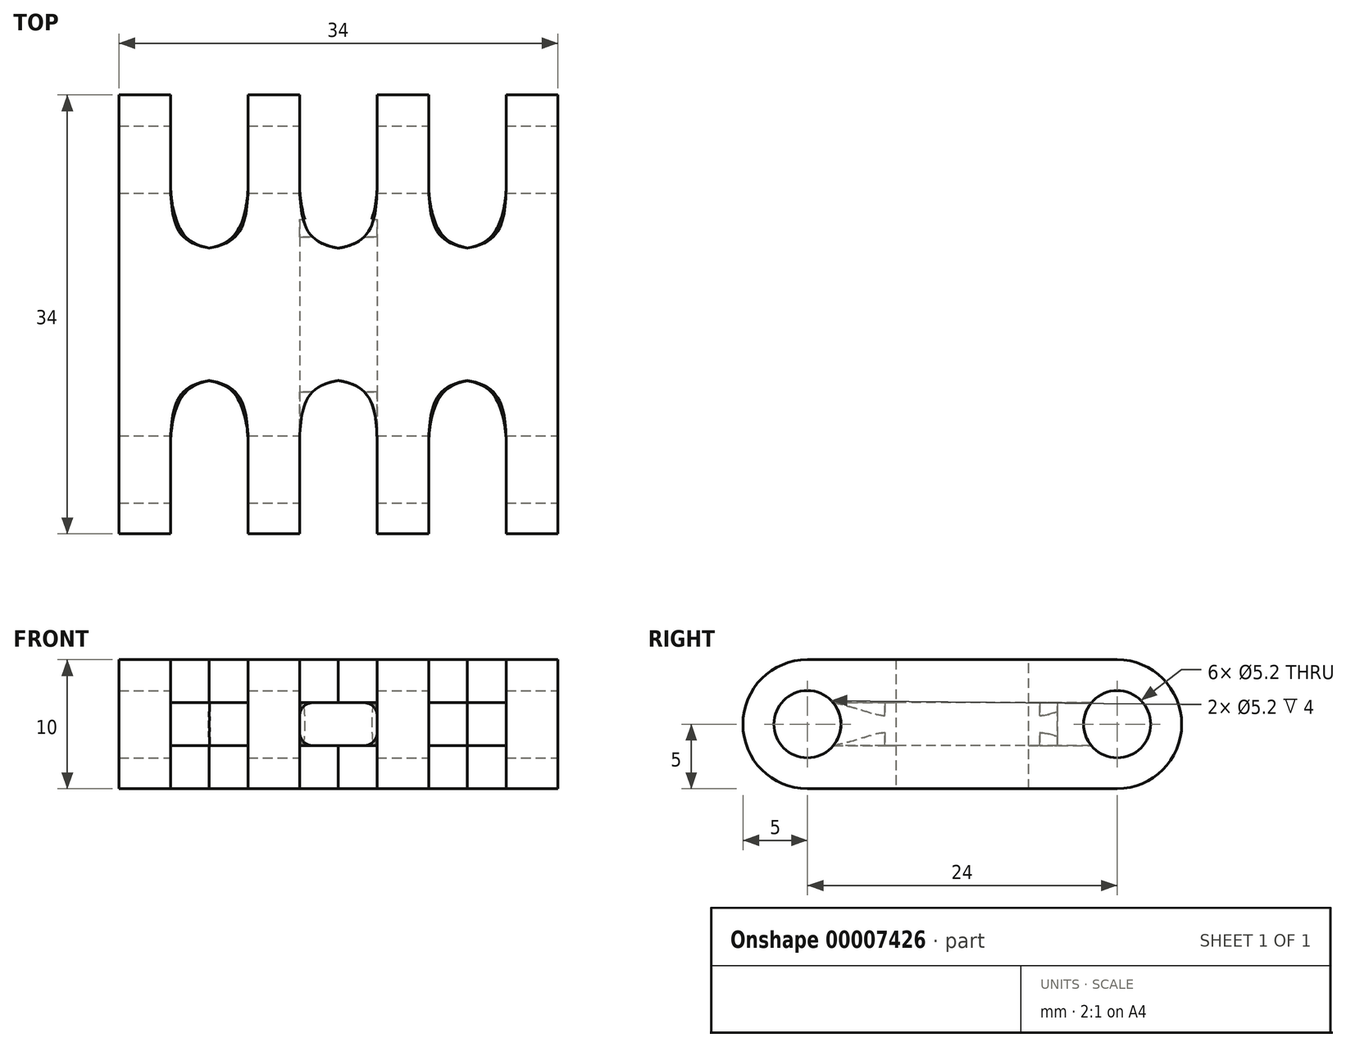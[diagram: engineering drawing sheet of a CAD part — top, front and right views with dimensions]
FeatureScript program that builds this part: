
annotation { "Feature Type Name" : "Feature", "Feature Type Description" : "" }
export const myFeature = defineFeature(function(context is Context, id is Id, definition is map)
    precondition{}
    {
        {
            var Q0;
            Q0=qCreatedBy(makeId("Front.planeOp"),FACE);
            var sketch = newSketch(context, id + "F0", { "sketchPlane" : qUnion([Q0])});
            skLineSegment(sketch, "E0.bottom", {"start": v(-16.45, 10) * mm, "end": v(17.55, 10) * mm});
            skLineSegment(sketch, "E0.top", {"start": v(-16.45, 0) * mm, "end": v(17.55, 0) * mm});
            skLineSegment(sketch, "E0.left", {"start": v(-16.45, 10) * mm, "end": v(-16.45, 0) * mm});
            skLineSegment(sketch, "E0.right", {"start": v(17.55, 10) * mm, "end": v(17.55, 0) * mm});
            skSolve(sketch);
        }
        {
            var Q0;
            Q0=makeQuery(id+"F0.imprint","IMPRINT",FACE,{"disambiguationData":[TD([[makeQuery(id+"F0.imprint","IMPRINT",EDGE,{"derivedFrom":sQuery(id+"F0.wireOp",EDGE,"E0.bottom")}),-1.0]])]});
            extrude(context, id + "F1", {"entities" : qUnion([Q0]), "depth" : 10 * mm});
        }
        {
            var Q0;
            {var subQ0=sQuery(id+"F0.wireOp",EDGE,"E0.bottom");var subQ1=sQuery(id+"F0.wireOp",EDGE,"E0.top");Q0=makeQuery(id+"F4.boolean.opBoolean","SPLIT",FACE,{"disambiguationData":[TD([makeQuery(id+"F4.opExtrude","SWEPT_FACE",FACE,{"disambiguationData":[OSD([sQuery(id+"F3.wireOp",EDGE,"E3.right")])]})])],"derivedFrom":makeQuery(id+"F1.opExtrude","CAP_FACE",FACE,{"disambiguationData":[OSD([subQ0,subQ1,sQuery(id+"F0.wireOp",EDGE,"E0.left"),sQuery(id+"F0.wireOp",EDGE,"E0.right")])],"isStart":false})});}
            cPlane(context, id + "F2", {"entities" : qUnion([Q0]), "cplaneType" : CPlaneType.OFFSET, "offset" : 5 * mm, "oppositeDirection" : true, "width" : 150 * mm, "height" : 150 * mm});
        }
        {
            var Q0;
            Q0=qCreatedBy(id+"F2.planeOp",FACE);
            var sketch = newSketch(context, id + "F3", { "sketchPlane" : qUnion([Q0])});
            skLineSegment(sketch, "E1.bottom", {"start": v(-16.45, 10) * mm, "end": v(-12.45, 10) * mm});
            skLineSegment(sketch, "E1.top", {"start": v(-16.45, 0) * mm, "end": v(-12.45, 0) * mm});
            skLineSegment(sketch, "E1.left", {"start": v(-16.45, 10) * mm, "end": v(-16.45, 0) * mm});
            skLineSegment(sketch, "E1.right", {"start": v(-12.45, 10) * mm, "end": v(-12.45, 0) * mm});
            skLineSegment(sketch, "E2.bottom", {"start": v(-6.45, 10) * mm, "end": v(-2.45, 10) * mm});
            skLineSegment(sketch, "E2.top", {"start": v(-6.45, 0) * mm, "end": v(-2.45, 0) * mm});
            skLineSegment(sketch, "E2.left", {"start": v(-6.45, 10) * mm, "end": v(-6.45, 0) * mm});
            skLineSegment(sketch, "E2.right", {"start": v(-2.45, 10) * mm, "end": v(-2.45, 0) * mm});
            skLineSegment(sketch, "E3.bottom", {"start": v(17.55, 10) * mm, "end": v(13.55, 10) * mm});
            skLineSegment(sketch, "E3.top", {"start": v(17.55, 0) * mm, "end": v(13.55, 0) * mm});
            skLineSegment(sketch, "E3.left", {"start": v(17.55, 10) * mm, "end": v(17.55, 0) * mm});
            skLineSegment(sketch, "E3.right", {"start": v(13.55, 10) * mm, "end": v(13.55, 0) * mm});
            skLineSegment(sketch, "E4.bottom", {"start": v(3.55, 10) * mm, "end": v(7.55, 10) * mm});
            skLineSegment(sketch, "E4.top", {"start": v(3.55, 0) * mm, "end": v(7.55, 0) * mm});
            skLineSegment(sketch, "E4.left", {"start": v(3.55, 10) * mm, "end": v(3.55, 0) * mm});
            skLineSegment(sketch, "E4.right", {"start": v(7.55, 10) * mm, "end": v(7.55, 0) * mm});
            skSolve(sketch);
        }
        {
            var Q0;
            Q0=makeQuery(id+"F3.imprint","IMPRINT",FACE,{"disambiguationData":[TD([[makeQuery(id+"F3.imprint","IMPRINT",EDGE,{"derivedFrom":sQuery(id+"F3.wireOp",EDGE,"E1.bottom")}),-1.0]])]});
            var Q1;
            Q1=makeQuery(id+"F3.imprint","IMPRINT",FACE,{"disambiguationData":[TD([[makeQuery(id+"F3.imprint","IMPRINT",EDGE,{"derivedFrom":sQuery(id+"F3.wireOp",EDGE,"E2.bottom")}),-1.0]])]});
            var Q2;
            Q2=makeQuery(id+"F3.imprint","IMPRINT",FACE,{"disambiguationData":[TD([[makeQuery(id+"F3.imprint","IMPRINT",EDGE,{"derivedFrom":sQuery(id+"F3.wireOp",EDGE,"E4.bottom")}),-1.0]])]});
            var Q3;
            Q3=makeQuery(id+"F3.imprint","IMPRINT",FACE,{"disambiguationData":[TD([[makeQuery(id+"F3.imprint","IMPRINT",EDGE,{"derivedFrom":sQuery(id+"F3.wireOp",EDGE,"E3.bottom")}),-1.0]])]});
            var Q4;
            Q4=makeQuery(id+"F3.imprint","IMPRINT",FACE,{"disambiguationData":[TD([[makeQuery(id+"F3.imprint","IMPRINT",EDGE,{"derivedFrom":sQuery(id+"F3.wireOp",EDGE,"E3.bottom")}),1.0]])]});
            extrude(context, id + "F4", {"entities" : qUnion([Q0, Q1, Q2, Q3, Q4]), "operationType" : NewBodyOperationType.ADD, "depth" : 24 * mm, "symmetric" : true});
        }
        {
            var Q0;
            Q0=makeQuery(id+"F4.boolean.opBoolean","MERGE",FACE,{"derivedFrom":[makeQuery(id+"F1.opExtrude","SWEPT_FACE",FACE,{"disambiguationData":[OSD([sQuery(id+"F0.wireOp",EDGE,"E0.right")])]}),makeQuery(id+"F4.opExtrude","SWEPT_FACE",FACE,{"disambiguationData":[OSD([sQuery(id+"F3.wireOp",EDGE,"E3.left")])]})]});
            var sketch = newSketch(context, id + "F5", { "sketchPlane" : qUnion([Q0])});
            skCircle(sketch, "E5", {"center": v(-17, 5) * mm, "radius": 5 * mm});
            skCircle(sketch, "E6", {"center": v(7, 5) * mm, "radius": 5 * mm});
            skSolve(sketch);
        }
        {
            var Q0;
            {var subQ0=sQuery(id+"F3.wireOp",EDGE,"E3.left");var subQ1=makeQuery(id+"F4.opExtrude","CAP_EDGE",EDGE,{"disambiguationData":[OSD([subQ0])],"isStart":false});Q0=makeQuery(id+"F5.imprint","IMPRINT",FACE,{"disambiguationData":[TD([[makeQuery(id+"F5.imprint","IMPRINT",EDGE,{"derivedFrom":subQ1}),-1.0]])]});}
            var Q1;
            {var subQ0=sQuery(id+"F3.wireOp",EDGE,"E3.left");var subQ1=makeQuery(id+"F4.opExtrude","CAP_EDGE",EDGE,{"disambiguationData":[OSD([subQ0])],"isStart":true});Q1=makeQuery(id+"F5.imprint","IMPRINT",FACE,{"disambiguationData":[TD([[makeQuery(id+"F5.imprint","IMPRINT",EDGE,{"derivedFrom":subQ1}),1.0]])]});}
            var Q2;
            {var subQ0=sQuery(id+"F3.wireOp",EDGE,"E3.left");var subQ1=makeQuery(id+"F4.opExtrude","CAP_EDGE",EDGE,{"disambiguationData":[OSD([subQ0])],"isStart":true});Q2=makeQuery(id+"F5.imprint","IMPRINT",FACE,{"disambiguationData":[TD([[makeQuery(id+"F5.imprint","IMPRINT",EDGE,{"derivedFrom":subQ1}),-1.0]])]});}
            var Q3;
            {var subQ0=sQuery(id+"F3.wireOp",EDGE,"E3.left");var subQ1=makeQuery(id+"F4.opExtrude","CAP_EDGE",EDGE,{"disambiguationData":[OSD([subQ0])],"isStart":false});Q3=makeQuery(id+"F5.imprint","IMPRINT",FACE,{"disambiguationData":[TD([[makeQuery(id+"F5.imprint","IMPRINT",EDGE,{"derivedFrom":subQ1}),1.0]])]});}
            extrude(context, id + "F6", {"entities" : qUnion([Q0, Q1, Q2, Q3]), "operationType" : NewBodyOperationType.ADD, "oppositeDirection" : true, "depth" : 34 * mm});
        }
        {
            var Q0;
            Q0=makeQuery(id+"F4.boolean.opBoolean","MERGE",FACE,{"derivedFrom":[makeQuery(id+"F1.opExtrude","SWEPT_FACE",FACE,{"disambiguationData":[OSD([sQuery(id+"F0.wireOp",EDGE,"E0.bottom")])]}),makeQuery(id+"F4.opExtrude","SWEPT_FACE",FACE,{"disambiguationData":[OSD([sQuery(id+"F3.wireOp",EDGE,"E1.bottom")])]}),makeQuery(id+"F4.opExtrude","SWEPT_FACE",FACE,{"disambiguationData":[OSD([sQuery(id+"F3.wireOp",EDGE,"E2.bottom")])]}),makeQuery(id+"F4.opExtrude","SWEPT_FACE",FACE,{"disambiguationData":[OSD([sQuery(id+"F3.wireOp",EDGE,"E3.bottom")])]}),makeQuery(id+"F4.opExtrude","SWEPT_FACE",FACE,{"disambiguationData":[OSD([sQuery(id+"F3.wireOp",EDGE,"E4.bottom")])]})]});
            var sketch = newSketch(context, id + "F7", { "sketchPlane" : qUnion([Q0])});
            skLineSegment(sketch, "E7.bottom", {"start": v(-12.45, -10) * mm, "end": v(-6.45, -10) * mm});
            skLineSegment(sketch, "E7.top", {"start": v(-12.45, -24.03) * mm, "end": v(-6.45, -24.03) * mm});
            skLineSegment(sketch, "E7.left", {"start": v(-12.45, -10) * mm, "end": v(-12.45, -24.03) * mm});
            skLineSegment(sketch, "E7.right", {"start": v(-6.45, -10) * mm, "end": v(-6.45, -24.03) * mm});
            skLineSegment(sketch, "E8.bottom", {"start": v(-2.45, -10) * mm, "end": v(3.55, -10) * mm});
            skLineSegment(sketch, "E8.top", {"start": v(-2.45, -24.03) * mm, "end": v(3.55, -24.03) * mm});
            skLineSegment(sketch, "E8.left", {"start": v(-2.45, -10) * mm, "end": v(-2.45, -24.03) * mm});
            skLineSegment(sketch, "E8.right", {"start": v(3.55, -10) * mm, "end": v(3.55, -24.03) * mm});
            skLineSegment(sketch, "E9.bottom", {"start": v(7.55, -10) * mm, "end": v(13.55, -10) * mm});
            skLineSegment(sketch, "E9.top", {"start": v(7.55, -24.03) * mm, "end": v(13.55, -24.03) * mm});
            skLineSegment(sketch, "E9.left", {"start": v(7.55, -10) * mm, "end": v(7.55, -24.03) * mm});
            skLineSegment(sketch, "E9.right", {"start": v(13.55, -10) * mm, "end": v(13.55, -24.03) * mm});
            skLineSegment(sketch, "E10.bottom", {"start": v(-12.45, 0) * mm, "end": v(-6.45, 0) * mm});
            skLineSegment(sketch, "E10.top", {"start": v(-12.45, 16.74) * mm, "end": v(-6.45, 16.74) * mm});
            skLineSegment(sketch, "E10.left", {"start": v(-12.45, 0) * mm, "end": v(-12.45, 16.74) * mm});
            skLineSegment(sketch, "E10.right", {"start": v(-6.45, 0) * mm, "end": v(-6.45, 16.74) * mm});
            skLineSegment(sketch, "E11.bottom", {"start": v(-2.45, 0) * mm, "end": v(3.55, 0) * mm});
            skLineSegment(sketch, "E11.top", {"start": v(-2.45, 16.6) * mm, "end": v(3.55, 16.6) * mm});
            skLineSegment(sketch, "E11.left", {"start": v(-2.45, 0) * mm, "end": v(-2.45, 16.6) * mm});
            skLineSegment(sketch, "E11.right", {"start": v(3.55, 0) * mm, "end": v(3.55, 16.6) * mm});
            skLineSegment(sketch, "E12.bottom", {"start": v(7.55, 0) * mm, "end": v(13.55, 0) * mm});
            skLineSegment(sketch, "E12.top", {"start": v(7.55, 16.45) * mm, "end": v(13.55, 16.45) * mm});
            skLineSegment(sketch, "E12.left", {"start": v(7.55, 0) * mm, "end": v(7.55, 16.45) * mm});
            skLineSegment(sketch, "E12.right", {"start": v(13.55, 0) * mm, "end": v(13.55, 16.45) * mm});
            skSolve(sketch);
        }
        {
            var Q0;
            {var subQ2=sQuery(id+"F7.wireOp",EDGE,"E10.bottom");Q0=makeQuery(id+"F7.imprint","IMPRINT",FACE,{"disambiguationData":[TD([[makeQuery(id+"F7.imprint","IMPRINT",EDGE,{"derivedFrom":subQ2}),1.0]])]});}
            var Q1;
            {var subQ2=sQuery(id+"F7.wireOp",EDGE,"E11.bottom");Q1=makeQuery(id+"F7.imprint","IMPRINT",FACE,{"disambiguationData":[TD([[makeQuery(id+"F7.imprint","IMPRINT",EDGE,{"derivedFrom":subQ2}),1.0]])]});}
            var Q2;
            {var subQ2=sQuery(id+"F7.wireOp",EDGE,"E12.bottom");Q2=makeQuery(id+"F7.imprint","IMPRINT",FACE,{"disambiguationData":[TD([[makeQuery(id+"F7.imprint","IMPRINT",EDGE,{"derivedFrom":subQ2}),1.0]])]});}
            var Q3;
            {var subQ2=sQuery(id+"F7.wireOp",EDGE,"E9.bottom");Q3=makeQuery(id+"F7.imprint","IMPRINT",FACE,{"disambiguationData":[TD([[makeQuery(id+"F7.imprint","IMPRINT",EDGE,{"derivedFrom":subQ2}),-1.0]])]});}
            var Q4;
            {var subQ2=sQuery(id+"F7.wireOp",EDGE,"E8.bottom");Q4=makeQuery(id+"F7.imprint","IMPRINT",FACE,{"disambiguationData":[TD([[makeQuery(id+"F7.imprint","IMPRINT",EDGE,{"derivedFrom":subQ2}),-1.0]])]});}
            var Q5;
            {var subQ2=sQuery(id+"F7.wireOp",EDGE,"E7.bottom");Q5=makeQuery(id+"F7.imprint","IMPRINT",FACE,{"disambiguationData":[TD([[makeQuery(id+"F7.imprint","IMPRINT",EDGE,{"derivedFrom":subQ2}),-1.0]])]});}
            extrude(context, id + "F8", {"entities" : qUnion([Q0, Q1, Q2, Q3, Q4, Q5]), "operationType" : NewBodyOperationType.REMOVE, "oppositeDirection" : true, "depth" : 25 * mm});
        }
        {
            var Q0;
            Q0=makeQuery(id+"F6.boolean.opBoolean","MERGE",FACE,{"derivedFrom":[makeQuery(id+"F4.boolean.opBoolean","MERGE",FACE,{"derivedFrom":[makeQuery(id+"F1.opExtrude","SWEPT_FACE",FACE,{"disambiguationData":[OSD([sQuery(id+"F0.wireOp",EDGE,"E0.right")])]}),makeQuery(id+"F4.opExtrude","SWEPT_FACE",FACE,{"disambiguationData":[OSD([sQuery(id+"F3.wireOp",EDGE,"E3.left")])]})]}),makeQuery(id+"F6.opExtrude","CAP_FACE",FACE,{"disambiguationData":[OSD([sQuery(id+"F5.wireOp",EDGE,"E5")])],"isStart":true}),makeQuery(id+"F6.opExtrude","CAP_FACE",FACE,{"disambiguationData":[OSD([sQuery(id+"F5.wireOp",EDGE,"E6")])],"isStart":true})]});
            var sketch = newSketch(context, id + "F9", { "sketchPlane" : qUnion([Q0])});
            skCircle(sketch, "E13", {"center": v(7, 5) * mm, "radius": 5 * mm});
            skCircle(sketch, "E14", {"center": v(-17, 5) * mm, "radius": 5 * mm});
            skCircle(sketch, "E15", {"center": v(-17, 5) * mm, "radius": 2.6 * mm});
            skCircle(sketch, "E16", {"center": v(7, 5) * mm, "radius": 2.6 * mm});
            skSolve(sketch);
        }
        {
            var Q0;
            Q0=makeQuery(id+"F9.imprint","IMPRINT",FACE,{"disambiguationData":[TD([[makeQuery(id+"F9.imprint","IMPRINT",EDGE,{"derivedFrom":sQuery(id+"F9.wireOp",EDGE,"E15")}),1.0]])]});
            var Q1;
            Q1=makeQuery(id+"F9.imprint","IMPRINT",FACE,{"disambiguationData":[TD([[makeQuery(id+"F9.imprint","IMPRINT",EDGE,{"derivedFrom":sQuery(id+"F9.wireOp",EDGE,"E16")}),1.0]])]});
            extrude(context, id + "F10", {"entities" : qUnion([Q0, Q1]), "operationType" : NewBodyOperationType.REMOVE, "endBound" : BoundingType.THROUGH_ALL, "oppositeDirection" : true, "depth" : 25 * mm});
        }
        {
            var Q0;
            Q0=makeQuery(id+"F4.boolean.opBoolean","INTERSECT",EDGE,{"derivedFrom":[makeQuery(id+"F1.opExtrude","CAP_FACE",FACE,{"disambiguationData":[OSD([sQuery(id+"F0.wireOp",EDGE,"E0.bottom"),sQuery(id+"F0.wireOp",EDGE,"E0.top"),sQuery(id+"F0.wireOp",EDGE,"E0.left"),sQuery(id+"F0.wireOp",EDGE,"E0.right")])],"isStart":true}),makeQuery(id+"F4.opExtrude","SWEPT_FACE",FACE,{"disambiguationData":[OSD([sQuery(id+"F3.wireOp",EDGE,"E3.right")])]})]});
            var Q1;
            Q1=makeQuery(id+"F4.boolean.opBoolean","INTERSECT",EDGE,{"derivedFrom":[makeQuery(id+"F1.opExtrude","CAP_FACE",FACE,{"disambiguationData":[OSD([sQuery(id+"F0.wireOp",EDGE,"E0.bottom"),sQuery(id+"F0.wireOp",EDGE,"E0.top"),sQuery(id+"F0.wireOp",EDGE,"E0.left"),sQuery(id+"F0.wireOp",EDGE,"E0.right")])],"isStart":true}),makeQuery(id+"F4.opExtrude","SWEPT_FACE",FACE,{"disambiguationData":[OSD([sQuery(id+"F3.wireOp",EDGE,"E4.right")])]})]});
            var Q2;
            Q2=makeQuery(id+"F4.boolean.opBoolean","INTERSECT",EDGE,{"derivedFrom":[makeQuery(id+"F1.opExtrude","CAP_FACE",FACE,{"disambiguationData":[OSD([sQuery(id+"F0.wireOp",EDGE,"E0.bottom"),sQuery(id+"F0.wireOp",EDGE,"E0.top"),sQuery(id+"F0.wireOp",EDGE,"E0.left"),sQuery(id+"F0.wireOp",EDGE,"E0.right")])],"isStart":true}),makeQuery(id+"F4.opExtrude","SWEPT_FACE",FACE,{"disambiguationData":[OSD([sQuery(id+"F3.wireOp",EDGE,"E2.right")])]})]});
            var Q3;
            Q3=makeQuery(id+"F4.boolean.opBoolean","INTERSECT",EDGE,{"derivedFrom":[makeQuery(id+"F1.opExtrude","CAP_FACE",FACE,{"disambiguationData":[OSD([sQuery(id+"F0.wireOp",EDGE,"E0.bottom"),sQuery(id+"F0.wireOp",EDGE,"E0.top"),sQuery(id+"F0.wireOp",EDGE,"E0.left"),sQuery(id+"F0.wireOp",EDGE,"E0.right")])],"isStart":true}),makeQuery(id+"F4.opExtrude","SWEPT_FACE",FACE,{"disambiguationData":[OSD([sQuery(id+"F3.wireOp",EDGE,"E4.left")])]})]});
            var Q4;
            Q4=makeQuery(id+"F4.boolean.opBoolean","INTERSECT",EDGE,{"derivedFrom":[makeQuery(id+"F1.opExtrude","CAP_FACE",FACE,{"disambiguationData":[OSD([sQuery(id+"F0.wireOp",EDGE,"E0.bottom"),sQuery(id+"F0.wireOp",EDGE,"E0.top"),sQuery(id+"F0.wireOp",EDGE,"E0.left"),sQuery(id+"F0.wireOp",EDGE,"E0.right")])],"isStart":true}),makeQuery(id+"F4.opExtrude","SWEPT_FACE",FACE,{"disambiguationData":[OSD([sQuery(id+"F3.wireOp",EDGE,"E2.left")])]})]});
            var Q5;
            Q5=makeQuery(id+"F4.boolean.opBoolean","INTERSECT",EDGE,{"derivedFrom":[makeQuery(id+"F1.opExtrude","CAP_FACE",FACE,{"disambiguationData":[OSD([sQuery(id+"F0.wireOp",EDGE,"E0.bottom"),sQuery(id+"F0.wireOp",EDGE,"E0.top"),sQuery(id+"F0.wireOp",EDGE,"E0.left"),sQuery(id+"F0.wireOp",EDGE,"E0.right")])],"isStart":true}),makeQuery(id+"F4.opExtrude","SWEPT_FACE",FACE,{"disambiguationData":[OSD([sQuery(id+"F3.wireOp",EDGE,"E1.right")])]})]});
            var Q6;
            Q6=makeQuery(id+"F4.boolean.opBoolean","INTERSECT",EDGE,{"derivedFrom":[makeQuery(id+"F1.opExtrude","CAP_FACE",FACE,{"disambiguationData":[OSD([sQuery(id+"F0.wireOp",EDGE,"E0.bottom"),sQuery(id+"F0.wireOp",EDGE,"E0.top"),sQuery(id+"F0.wireOp",EDGE,"E0.left"),sQuery(id+"F0.wireOp",EDGE,"E0.right")])],"isStart":false}),makeQuery(id+"F4.opExtrude","SWEPT_FACE",FACE,{"disambiguationData":[OSD([sQuery(id+"F3.wireOp",EDGE,"E4.right")])]})]});
            var Q7;
            Q7=makeQuery(id+"F4.boolean.opBoolean","INTERSECT",EDGE,{"derivedFrom":[makeQuery(id+"F1.opExtrude","CAP_FACE",FACE,{"disambiguationData":[OSD([sQuery(id+"F0.wireOp",EDGE,"E0.bottom"),sQuery(id+"F0.wireOp",EDGE,"E0.top"),sQuery(id+"F0.wireOp",EDGE,"E0.left"),sQuery(id+"F0.wireOp",EDGE,"E0.right")])],"isStart":false}),makeQuery(id+"F4.opExtrude","SWEPT_FACE",FACE,{"disambiguationData":[OSD([sQuery(id+"F3.wireOp",EDGE,"E2.right")])]})]});
            var Q8;
            Q8=makeQuery(id+"F4.boolean.opBoolean","INTERSECT",EDGE,{"derivedFrom":[makeQuery(id+"F1.opExtrude","CAP_FACE",FACE,{"disambiguationData":[OSD([sQuery(id+"F0.wireOp",EDGE,"E0.bottom"),sQuery(id+"F0.wireOp",EDGE,"E0.top"),sQuery(id+"F0.wireOp",EDGE,"E0.left"),sQuery(id+"F0.wireOp",EDGE,"E0.right")])],"isStart":false}),makeQuery(id+"F4.opExtrude","SWEPT_FACE",FACE,{"disambiguationData":[OSD([sQuery(id+"F3.wireOp",EDGE,"E1.right")])]})]});
            var Q9;
            Q9=makeQuery(id+"F4.boolean.opBoolean","INTERSECT",EDGE,{"derivedFrom":[makeQuery(id+"F1.opExtrude","CAP_FACE",FACE,{"disambiguationData":[OSD([sQuery(id+"F0.wireOp",EDGE,"E0.bottom"),sQuery(id+"F0.wireOp",EDGE,"E0.top"),sQuery(id+"F0.wireOp",EDGE,"E0.left"),sQuery(id+"F0.wireOp",EDGE,"E0.right")])],"isStart":false}),makeQuery(id+"F4.opExtrude","SWEPT_FACE",FACE,{"disambiguationData":[OSD([sQuery(id+"F3.wireOp",EDGE,"E2.left")])]})]});
            var Q10;
            Q10=makeQuery(id+"F4.boolean.opBoolean","INTERSECT",EDGE,{"derivedFrom":[makeQuery(id+"F1.opExtrude","CAP_FACE",FACE,{"disambiguationData":[OSD([sQuery(id+"F0.wireOp",EDGE,"E0.bottom"),sQuery(id+"F0.wireOp",EDGE,"E0.top"),sQuery(id+"F0.wireOp",EDGE,"E0.left"),sQuery(id+"F0.wireOp",EDGE,"E0.right")])],"isStart":false}),makeQuery(id+"F4.opExtrude","SWEPT_FACE",FACE,{"disambiguationData":[OSD([sQuery(id+"F3.wireOp",EDGE,"E4.left")])]})]});
            var Q11;
            Q11=makeQuery(id+"F4.boolean.opBoolean","INTERSECT",EDGE,{"derivedFrom":[makeQuery(id+"F1.opExtrude","CAP_FACE",FACE,{"disambiguationData":[OSD([sQuery(id+"F0.wireOp",EDGE,"E0.bottom"),sQuery(id+"F0.wireOp",EDGE,"E0.top"),sQuery(id+"F0.wireOp",EDGE,"E0.left"),sQuery(id+"F0.wireOp",EDGE,"E0.right")])],"isStart":false}),makeQuery(id+"F4.opExtrude","SWEPT_FACE",FACE,{"disambiguationData":[OSD([sQuery(id+"F3.wireOp",EDGE,"E3.right")])]})]});
            fillet(context, id + "F11", {"entities" : qUnion([Q0, Q1, Q2, Q3, Q4, Q5, Q6, Q7, Q8, Q9, Q10, Q11]), "radius" : 5 * mm, "tangentPropagation" : true, "rho" : .6, "crossSection" : FilletCrossSection.CONIC, "allowEdgeOverflow" : false});
        }
        {
            var Q0;
            Q0=makeQuery(id+"F1.opExtrude","SWEPT_BODY",BODY,{"disambiguationData":[OSD([sQuery(id+"F0.wireOp",EDGE,"E0.bottom"),sQuery(id+"F0.wireOp",EDGE,"E0.top"),sQuery(id+"F0.wireOp",EDGE,"E0.left"),sQuery(id+"F0.wireOp",EDGE,"E0.right")])]});
            transform(context, id + "F12", {"entities" : qUnion([Q0]), "transformType" : TransformType.TRANSLATION_3D, "dx" : -.533 * mm, "dy" : 5.13 * mm, "dz" : 0 * mm, "makeCopy" : false});
        }
        {
            var Q0;
            Q0=qCreatedBy(id+"F2.planeOp",FACE);
            var sketch = newSketch(context, id + "F13", { "sketchPlane" : qUnion([Q0])});
            skFitSpline(sketch, "E17.0.0", {"points": [v(0.02, 6.66) * mm, v(-0.98, 6.66) * mm, v(-1.98, 6.66) * mm, v(-2.98, 6.66) * mm]});
            skFitSpline(sketch, "E17.0.1", {"points": [v(-2.98, 6.66) * mm, v(-2.98, 5.55) * mm, v(-2.98, 4.45) * mm, v(-2.98, 3.34) * mm]});
            skFitSpline(sketch, "E17.0.2", {"points": [v(-2.98, 3.34) * mm, v(-1.98, 3.34) * mm, v(-0.98, 3.34) * mm, v(0.02, 3.34) * mm]});
            skFitSpline(sketch, "E17.1.0", {"points": [v(3.02, 6.66) * mm, v(2.02, 6.66) * mm, v(1.02, 6.66) * mm, v(0.02, 6.66) * mm]});
            skFitSpline(sketch, "E17.1.2", {"points": [v(0.02, 3.34) * mm, v(1.02, 3.34) * mm, v(2.02, 3.34) * mm, v(3.02, 3.34) * mm]});
            skFitSpline(sketch, "E17.1.3", {"points": [v(3.02, 3.34) * mm, v(3.02, 4.45) * mm, v(3.02, 5.55) * mm, v(3.02, 6.66) * mm]});
            skSolve(sketch);
        }
        {
            var Q0;
            Q0=makeQuery(id+"F13.imprint","IMPRINT",FACE,{"disambiguationData":[TD([[makeQuery(id+"F13.imprint","IMPRINT",EDGE,{"derivedFrom":sQuery(id+"F13.wireOp",EDGE,"E17.0.0")}),1.0]])]});
            extrude(context, id + "F14", {"entities" : qUnion([Q0]), "operationType" : NewBodyOperationType.REMOVE, "oppositeDirection" : true, "depth" : 25 * mm, "symmetric" : true});
        }
        {
            var Q0;
            Q0=makeQuery(id+"F14.boolean.opBoolean","COPY",EDGE,{"derivedFrom":makeQuery(id+"F14.opExtrude","SWEPT_EDGE",EDGE,{"disambiguationData":[OSD([sQuery(id+"F13.wireOp",EDGE,"E17.1.0"),sQuery(id+"F13.wireOp",EDGE,"E17.1.3")])]})});
            var Q1;
            Q1=makeQuery(id+"F14.boolean.opBoolean","COPY",EDGE,{"derivedFrom":makeQuery(id+"F14.opExtrude","SWEPT_EDGE",EDGE,{"disambiguationData":[OSD([sQuery(id+"F13.wireOp",EDGE,"E17.0.0"),sQuery(id+"F13.wireOp",EDGE,"E17.0.1")])]})});
            var Q2;
            Q2=makeQuery(id+"F14.boolean.opBoolean","COPY",EDGE,{"derivedFrom":makeQuery(id+"F14.opExtrude","SWEPT_EDGE",EDGE,{"disambiguationData":[OSD([sQuery(id+"F13.wireOp",EDGE,"E17.0.1"),sQuery(id+"F13.wireOp",EDGE,"E17.0.2")])]})});
            var Q3;
            Q3=makeQuery(id+"F14.boolean.opBoolean","COPY",EDGE,{"derivedFrom":makeQuery(id+"F14.opExtrude","SWEPT_EDGE",EDGE,{"disambiguationData":[OSD([sQuery(id+"F13.wireOp",EDGE,"E17.1.2"),sQuery(id+"F13.wireOp",EDGE,"E17.1.3")])]})});
            fillet(context, id + "F15", {"entities" : qUnion([Q0, Q1, Q2, Q3]), "radius" : 1 * mm, "tangentPropagation" : true, "allowEdgeOverflow" : false});
        }
    });
